# Revit family: Поли-Групп_ЗадвижкаКлиноваяEAZ-МК-F5(ВS)_DN350-1600
name_source: partatom
category: Арматура трубопроводов
units: mm (PartAtom-declared; Revit-internal decimal feet)

## family parameters
Всегда вертикально = Да
На основе рабочей плоскости = Нет
Общий = Нет
При загрузке вырезать с полостями = Нет
Размер круглого соединителя = Использовать диаметр
Тип детали = Клапан - Вставляется

## types (24) — shared parameters
ADSK_URL страницы изделия = https://www.polycorr.ru
ADSK_Версия Revit = 2019
ADSK_Единица измерения = шт
ADSK_Завод-изготовитель = ООО ПК «Поли-Групп»
ADSK_Количество = 1
ADSK_Материал = Высокопрочный чугун GGG-40
ADSK_Материал наименование = Высокопрочный чугун с шаровидным графитом (GGG-40)
Kv = 1.0 м³/ч
Класс герметичности = А по ГОСТ Р 9544-2015
Материал Диска = Высокопрочный чугун с шаровидным графитом (GGG-40)
Материал уплотнителя = PTFE
Назначение = Для установки в качестве запорного устройства на трубопроводах
Покрытие = Высококачественное эпоксидное покрытие толщиной 300 мкм
Рабочая среда = Техническая вода, канализационные стоки, морская вода
Разработчик = https://3dbim.pro
Срок службы = 50 лет
ТВ = Поли-Групп_ЗадвижкаКлиноваяEAZ-МК-F5(ВS)_DN350-1600
Температура рабочей среды = 0 до +70°С
Тип привода = Редуктор
Тип присоединения = Фланцевое

## per-type parameters (varying)
- 350-10: A=756 мм; ADSK_Марка=EAZ-GV-3-F5 DN350 PN10; ADSK_Масса=276; ADSK_Масса_Текст=276; ADSK_Наименование=Задвижка клиновая с металлическим уплотнением EAZ MK F5 для сточных вод фланцевая DN350 PN10; ADSK_Наименование краткое=Задвижка клиновая EAZ MK F5 DN350 PN10; D=505 мм; D1=460 мм; D2=429 мм; DN=350 мм; D_Наружный=359 мм; H1=270 мм; H2=976 мм; L=550 мм; L1=270 мм; L2=81 мм; PN=10.0 бары; R=21 мм; R1=206 мм; b=25 мм; d1=88 мм; f=4 мм; h2=683 мм; l1=330 мм; l2=358 мм; l3=495 мм; t=68 мм; Габаритные размеры=505х550х1246; Корпус_Глубина=605 мм; с=18 мм
- 400-10: A=836 мм; ADSK_Марка=EAZ-GV-3-F5 DN400 PN10; ADSK_Масса=330; ADSK_Масса_Текст=330; ADSK_Наименование=Задвижка клиновая с металлическим уплотнением EAZ MK F5 для сточных вод фланцевая DN400 PN10; ADSK_Наименование краткое=Задвижка клиновая EAZ MK F5 DN400 PN10; D=565 мм; D1=515 мм; D2=480 мм; DN=400 мм; D_Наружный=409 мм; H1=300 мм; H2=1068 мм; L=600 мм; L1=300 мм; L2=90 мм; PN=10.0 бары; R=21 мм; R1=206 мм; b=25 мм; d1=100 мм; f=4 мм; h2=748 мм; l1=360 мм; l2=390 мм; l3=540 мм; t=75 мм; Габаритные размеры=565х600х1368; Корпус_Глубина=669 мм; с=18 мм
- 450-10: A=916 мм; ADSK_Марка=EAZ-GV-3-F5 D450 PN10; ADSK_Масса=419; ADSK_Масса_Текст=419; ADSK_Наименование=Задвижка клиновая с металлическим уплотнением EAZ MK F5 для сточных вод фланцевая DN450 PN10; ADSK_Наименование краткое=Задвижка клиновая EAZ MK F5 DN450 PN10; D=615 мм; D1=565 мм; D2=530 мм; DN=450 мм; D_Наружный=459 мм; H1=330 мм; H2=1180 мм; L=650 мм; L1=330 мм; L2=99 мм; PN=10.0 бары; R=28 мм; R1=275 мм; b=26 мм; d1=113 мм; f=4 мм; h2=826 мм; l1=390 мм; l2=423 мм; l3=585 мм; t=83 мм; Габаритные размеры=615х650х1510; Корпус_Глубина=733 мм; с=23 мм
- 500-10: A=996 мм; ADSK_Марка=EAZ-GV-3-F5 DN500 PN10; ADSK_Масса=655; ADSK_Масса_Текст=655; ADSK_Наименование=Задвижка клиновая с металлическим уплотнением EAZ MK F5 для сточных вод фланцевая DN500 PN10; ADSK_Наименование краткое=Задвижка клиновая EAZ MK F5 DN500 PN10; D=670 мм; D1=620 мм; D2=582 мм; DN=500 мм; D_Наружный=509 мм; H1=370 мм; H2=1247 мм; L=700 мм; L1=370 мм; L2=111 мм; PN=10.0 бары; R=28 мм; R1=275 мм; b=27 мм; d1=125 мм; f=4 мм; h2=873 мм; l1=420 мм; l2=455 мм; l3=630 мм; t=87 мм; Габаритные размеры=670х700х1617; Корпус_Глубина=797 мм; с=35 мм
- 600-10: A=1076 мм; ADSK_Марка=EAZ-GV-3-F5 DN600 PN10; ADSK_Масса=775; ADSK_Масса_Текст=775; ADSK_Наименование=Задвижка клиновая с металлическим уплотнением EAZ MK F5 для сточных вод фланцевая DN600 PN10; ADSK_Наименование краткое=Задвижка клиновая EAZ MK F5 DN600 PN10; D=780 мм; D1=725 мм; D2=682 мм; DN=600 мм; D_Наружный=609 мм; H1=430 мм; H2=1416 мм; L=800 мм; L1=430 мм; L2=129 мм; PN=10.0 бары; R=28 мм; R1=275 мм; b=30 мм; d1=150 мм; f=5 мм; h2=991 мм; l1=480 мм; l2=520 мм; l3=720 мм; t=99 мм; Габаритные размеры=780х800х1846; Корпус_Глубина=861 мм; с=40 мм
- 700-10: A=1156 мм; ADSK_Марка=EAZ-GV-3-F5 DN700 PN10; ADSK_Масса=1700; ADSK_Масса_Текст=1700; ADSK_Наименование=Задвижка клиновая с металлическим уплотнением EAZ MK F5 для сточных вод фланцевая DN700 PN10; ADSK_Наименование краткое=Задвижка клиновая EAZ MK F5 DN700 PN10; D=895 мм; D1=840 мм; D2=794 мм; DN=700 мм; D_Наружный=709 мм; H1=495 мм; H2=1808 мм; L=900 мм; L1=495 мм; L2=149 мм; PN=10.0 бары; R=31 мм; R1=307 мм; b=33 мм; d1=175 мм; f=5 мм; h2=1266 мм; l1=540 мм; l2=585 мм; l3=810 мм; t=127 мм; Габаритные размеры=895х900х2303; Корпус_Глубина=925 мм; с=48 мм
- 800-10: A=1242 мм; ADSK_Марка=EAZ-GV-3-F5 DN800 PN10; ADSK_Масса=2245; ADSK_Масса_Текст=2245; ADSK_Наименование=Задвижка клиновая с металлическим уплотнением EAZ MK F5 для сточных вод фланцевая DN800 PN10; ADSK_Наименование краткое=Задвижка клиновая EAZ MK F5 DN800 PN10; D=1015 мм; D1=950 мм; D2=901 мм; DN=800 мм; D_Наружный=809 мм; H1=540 мм; H2=1953 мм; L=1000 мм; L1=540 мм; L2=162 мм; PN=10.0 бары; R=33 мм; R1=330 мм; b=35 мм; d1=200 мм; f=5 мм; h2=1367 мм; l1=600 мм; l2=650 мм; l3=900 мм; t=137 мм; Габаритные размеры=1015х1000х2493; Корпус_Глубина=994 мм; с=33 мм
- 900-10: A=1423 мм; ADSK_Марка=EAZ-GV-3-F5 DN900 PN10; ADSK_Масса=3110; ADSK_Масса_Текст=3110; ADSK_Наименование=Задвижка клиновая с металлическим уплотнением EAZ MK F5 для сточных вод фланцевая DN900 PN10; ADSK_Наименование краткое=Задвижка клиновая EAZ MK F5 DN900 PN10; D=1115 мм; D1=1050 мм; D2=1001 мм; DN=900 мм; D_Наружный=909 мм; H1=645 мм; H2=2132 мм; L=1100 мм; L1=600 мм; L2=180 мм; PN=10.0 бары; R=37 мм; R1=370 мм; b=38 мм; d1=225 мм; f=5 мм; h2=1492 мм; l1=660 мм; l2=715 мм; l3=990 мм; t=149 мм; Габаритные размеры=1115х1100х2777; Корпус_Глубина=1138 мм; с=88 мм
- 1000-10: A=1448 мм; ADSK_Марка=EAZ-GV-3-F5 DN1000 PN10; ADSK_Масса=3510; ADSK_Масса_Текст=3510; ADSK_Наименование=Задвижка клиновая с металлическим уплотнением EAZ MK F5 для сточных вод фланцевая DN1000 PN10; ADSK_Наименование краткое=Задвижка клиновая EAZ MK F5 DN1000 PN10; D=1230 мм; D1=1160 мм; D2=1112 мм; DN=1000 мм; D_Наружный=1009 мм; H1=680 мм; H2=2362 мм; L=1200 мм; L1=680 мм; L2=204 мм; PN=10.0 бары; R=39 мм; R1=390 мм; b=40 мм; d1=250 мм; f=5 мм; h2=1653 мм; l1=720 мм; l2=780 мм; l3=1080 мм; t=165 мм; Габаритные размеры=1230х1200х3042; Корпус_Глубина=1158 мм; с=65 мм
- 1200-10: A=1625 мм; ADSK_Марка=EAZ-GV-3-F5 DN1200 PN10; ADSK_Масса=5180; ADSK_Масса_Текст=5180; ADSK_Наименование=Задвижка клиновая с металлическим уплотнением EAZ MK F5 для сточных вод фланцевая DN1200 PN10; ADSK_Наименование краткое=Задвижка клиновая EAZ MK F5 DN1200 PN10; D=1455 мм; D1=1380 мм; D2=1328 мм; DN=1200 мм; D_Наружный=1209 мм; H1=800 мм; H2=2652 мм; L=1400 мм; L1=800 мм; L2=240 мм; PN=10.0 бары; R=43 мм; R1=430 мм; b=45 мм; d1=300 мм; f=5 мм; h2=1856 мм; l1=840 мм; l2=910 мм; l3=1260 мм; t=186 мм; Габаритные размеры=1455х1400х3452; Корпус_Глубина=1300 мм; с=73 мм
- 1400-10: A=1860 мм; ADSK_Марка=EAZ-GV-3-F5 DN1400 PN10; ADSK_Масса=7128; ADSK_Масса_Текст=7128; ADSK_Наименование=Задвижка клиновая с металлическим уплотнением EAZ MK F5 для сточных вод фланцевая DN1400 PN10; ADSK_Наименование краткое=Задвижка клиновая EAZ MK F5 DN1400 PN10; D=1675 мм; D1=1590 мм; D2=1530 мм; DN=1400 мм; D_Наружный=1409 мм; H1=870 мм; H2=2972 мм; L=1600 мм; L1=870 мм; L2=261 мм; PN=10.0 бары; R=51 мм; R1=510 мм; b=46 мм; d1=350 мм; f=5 мм; h2=2080 мм; l1=960 мм; l2=1040 мм; l3=1440 мм; t=208 мм; Габаритные размеры=1675х1600х3842; Корпус_Глубина=1488 мм; с=33 мм
- 1600-10: A=2065 мм; ADSK_Марка=EAZ-GV-3-F5 DN1600 PN10; ADSK_Масса=10200; ADSK_Масса_Текст=10200; ADSK_Наименование=Задвижка клиновая с металлическим уплотнением EAZ MK F5 для сточных вод фланцевая DN1600 PN10; ADSK_Наименование краткое=Задвижка клиновая EAZ MK F5 DN1600 PN10; D=1915 мм; D1=1820 мм; D2=1750 мм; DN=1600 мм; D_Наружный=1609 мм; H1=1000 мм; H2=3380 мм; L=1600 мм; L1=1000 мм; L2=300 мм; PN=10.0 бары; R=63 мм; R1=630 мм; b=49 мм; d1=400 мм; f=5 мм; h2=2366 мм; l1=960 мм; l2=1040 мм; l3=1440 мм; t=237 мм; Габаритные размеры=1915х1600х4380; Корпус_Глубина=1652 мм; с=43 мм
- 350-16: A=756 мм; ADSK_Марка=EAZ-GV-3-F5 DN350 PN16; ADSK_Масса=285; ADSK_Масса_Текст=285; ADSK_Наименование=Задвижка клиновая с металлическим уплотнением EAZ MK F5 для сточных вод фланцевая DN350 PN16; ADSK_Наименование краткое=Задвижка клиновая EAZ MK F5 DN350 PN16; D=520 мм; D1=470 мм; D2=429 мм; DN=350 мм; D_Наружный=359 мм; H1=270 мм; H2=976 мм; L=550 мм; L1=270 мм; L2=81 мм; PN=16.0 бары; R=21 мм; R1=206 мм; b=27 мм; d1=88 мм; f=4 мм; h2=683 мм; l1=330 мм; l2=358 мм; l3=495 мм; t=68 мм; Габаритные размеры=520х550х1246; Корпус_Глубина=605 мм; с=10 мм
- 400-16: A=836 мм; ADSK_Марка=EAZ-GV-3-F5 DN400 PN16; ADSK_Масса=335; ADSK_Масса_Текст=335; ADSK_Наименование=Задвижка клиновая с металлическим уплотнением EAZ MK F5 для сточных вод фланцевая DN400 PN16; ADSK_Наименование краткое=Задвижка клиновая EAZ MK F5 DN400 PN16; D=580 мм; D1=525 мм; D2=480 мм; DN=400 мм; D_Наружный=409 мм; H1=300 мм; H2=1068 мм; L=600 мм; L1=300 мм; L2=90 мм; PN=16.0 бары; R=21 мм; R1=206 мм; b=28 мм; d1=100 мм; f=4 мм; h2=748 мм; l1=360 мм; l2=390 мм; l3=540 мм; t=75 мм; Габаритные размеры=580х600х1368; Корпус_Глубина=669 мм; с=10 мм
- 450-16: A=916 мм; ADSK_Марка=EAZ-GV-3-F5 DN450 PN16; ADSK_Масса=425; ADSK_Масса_Текст=425; ADSK_Наименование=Задвижка клиновая с металлическим уплотнением EAZ MK F5 для сточных вод фланцевая DN450 PN16; ADSK_Наименование краткое=Задвижка клиновая EAZ MK F5 DN450 PN16; D=640 мм; D1=585 мм; D2=548 мм; DN=450 мм; D_Наружный=459 мм; H1=330 мм; H2=1180 мм; L=650 мм; L1=330 мм; L2=99 мм; PN=16.0 бары; R=28 мм; R1=275 мм; b=30 мм; d1=113 мм; f=4 мм; h2=826 мм; l1=390 мм; l2=423 мм; l3=585 мм; t=83 мм; Габаритные размеры=640х650х1510; Корпус_Глубина=733 мм; с=10 мм
- 500-16: A=996 мм; ADSK_Марка=EAZ-GV-3-F5 DN500 PN16; ADSK_Масса=668; ADSK_Масса_Текст=668; ADSK_Наименование=Задвижка клиновая с металлическим уплотнением EAZ MK F5 для сточных вод фланцевая DN500 PN16; ADSK_Наименование краткое=Задвижка клиновая EAZ MK F5 DN500 PN16; D=715 мм; D1=650 мм; D2=609 мм; DN=500 мм; D_Наружный=509 мм; H1=370 мм; H2=1247 мм; L=700 мм; L1=370 мм; L2=111 мм; PN=16.0 бары; R=28 мм; R1=275 мм; b=32 мм; d1=125 мм; f=4 мм; h2=873 мм; l1=420 мм; l2=455 мм; l3=630 мм; t=87 мм; Габаритные размеры=715х700х1617; Корпус_Глубина=797 мм; с=13 мм
- 600-16: A=1076 мм; ADSK_Марка=EAZ-GV-3-F5 DN600 PN16; ADSK_Масса=790; ADSK_Масса_Текст=790; ADSK_Наименование=Задвижка клиновая с металлическим уплотнением EAZ MK F5 для сточных вод фланцевая DN600 PN16; ADSK_Наименование краткое=Задвижка клиновая EAZ MK F5 DN600 PN16; D=840 мм; D1=770 мм; D2=720 мм; DN=600 мм; D_Наружный=609 мм; H1=430 мм; H2=1416 мм; L=800 мм; L1=430 мм; L2=129 мм; PN=16.0 бары; R=28 мм; R1=275 мм; b=36 мм; d1=150 мм; f=5 мм; h2=991 мм; l1=480 мм; l2=520 мм; l3=720 мм; t=99 мм; Габаритные размеры=840х800х1846; Корпус_Глубина=861 мм; с=10 мм
- 700-16: A=1156 мм; ADSK_Марка=EAZ-GV-3-F5 DN700 PN16; ADSK_Масса=1765; ADSK_Масса_Текст=1765; ADSK_Наименование=Задвижка клиновая с металлическим уплотнением EAZ MK F5 для сточных вод фланцевая DN700 PN16; ADSK_Наименование краткое=Задвижка клиновая EAZ MK F5 DN700 PN16; D=910 мм; D1=840 мм; D2=794 мм; DN=700 мм; D_Наружный=709 мм; H1=495 мм; H2=1808 мм; L=900 мм; L1=495 мм; L2=149 мм; PN=16.0 бары; R=31 мм; R1=307 мм; b=40 мм; d1=175 мм; f=5 мм; h2=1266 мм; l1=540 мм; l2=585 мм; l3=810 мм; t=127 мм; Габаритные размеры=910х900х2303; Корпус_Глубина=925 мм; с=40 мм
- 800-16: A=1242 мм; ADSK_Марка=EAZ-GV-3-F5 DN800 PN16; ADSK_Масса=2460; ADSK_Масса_Текст=2460; ADSK_Наименование=Задвижка клиновая с металлическим уплотнением EAZ MK F5 для сточных вод фланцевая DN800 PN16; ADSK_Наименование краткое=Задвижка клиновая EAZ MK F5 DN800 PN16; D=1025 мм; D1=950 мм; D2=901 мм; DN=800 мм; D_Наружный=809 мм; H1=540 мм; H2=1953 мм; L=1000 мм; L1=540 мм; L2=162 мм; PN=16.0 бары; R=33 мм; R1=330 мм; b=43 мм; d1=200 мм; f=5 мм; h2=1367 мм; l1=600 мм; l2=650 мм; l3=900 мм; t=137 мм; Габаритные размеры=1025х1000х2493; Корпус_Глубина=994 мм; с=28 мм
- 900-16: A=1423 мм; ADSK_Марка=EAZ-GV-3-F5 DN900 PN16; ADSK_Масса=3160; ADSK_Масса_Текст=3160; ADSK_Наименование=Задвижка клиновая с металлическим уплотнением EAZ MK F5 для сточных вод фланцевая DN900 PN16; ADSK_Наименование краткое=Задвижка клиновая EAZ MK F5 DN900 PN16; D=1125 мм; D1=1050 мм; D2=1001 мм; DN=900 мм; D_Наружный=909 мм; H1=645 мм; H2=2132 мм; L=1100 мм; L1=600 мм; L2=180 мм; PN=16.0 бары; R=37 мм; R1=370 мм; b=47 мм; d1=225 мм; f=5 мм; h2=1492 мм; l1=660 мм; l2=715 мм; l3=990 мм; t=149 мм; Габаритные размеры=1125х1100х2777; Корпус_Глубина=1138 мм; с=83 мм
- 1000-16: A=1448 мм; ADSK_Марка=EAZ-GV-3-F5 DN1000 PN16; ADSK_Масса=3625; ADSK_Масса_Текст=3625; ADSK_Наименование=Задвижка клиновая с металлическим уплотнением EAZ MK F5 для сточных вод фланцевая DN1000 PN16; ADSK_Наименование краткое=Задвижка клиновая EAZ MK F5 DN1000 PN16; D=1255 мм; D1=1160 мм; D2=1112 мм; DN=1000 мм; D_Наружный=1009 мм; H1=680 мм; H2=2362 мм; L=1200 мм; L1=680 мм; L2=204 мм; PN=16.0 бары; R=39 мм; R1=390 мм; b=50 мм; d1=250 мм; f=5 мм; h2=1653 мм; l1=720 мм; l2=780 мм; l3=1080 мм; t=165 мм; Габаритные размеры=1255х1200х3042; Корпус_Глубина=1158 мм; с=53 мм
- 1200-16: A=1625 мм; ADSK_Марка=EAZ-GV-3-F5 DN1200 PN16; ADSK_Масса=5250; ADSK_Масса_Текст=5250; ADSK_Наименование=Задвижка клиновая с металлическим уплотнением EAZ MK F5 для сточных вод фланцевая DN1200 PN16; ADSK_Наименование краткое=Задвижка клиновая EAZ MK F5 DN1200 PN16; D=1485 мм; D1=1380 мм; D2=1328 мм; DN=1200 мм; D_Наружный=1209 мм; H1=800 мм; H2=2652 мм; L=1400 мм; L1=800 мм; L2=240 мм; PN=16.0 бары; R=43 мм; R1=430 мм; b=57 мм; d1=300 мм; f=5 мм; h2=1856 мм; l1=840 мм; l2=910 мм; l3=1260 мм; t=186 мм; Габаритные размеры=1485х1400х3452; Корпус_Глубина=1300 мм; с=58 мм
- 1400-16: A=1860 мм; ADSK_Марка=EAZ-GV-3-F5 DN1400 PN16; ADSK_Масса=7980; ADSK_Масса_Текст=7980; ADSK_Наименование=Задвижка клиновая с металлическим уплотнением EAZ MK F5 для сточных вод фланцевая DN1400 PN16; ADSK_Наименование краткое=Задвижка клиновая EAZ MK F5 DN1400 PN16; D=1685 мм; D1=1590 мм; D2=1530 мм; DN=1400 мм; D_Наружный=1409 мм; H1=870 мм; H2=3010 мм; L=1600 мм; L1=870 мм; L2=261 мм; PN=16.0 бары; R=51 мм; R1=510 мм; b=60 мм; d1=350 мм; f=5 мм; h2=2107 мм; l1=960 мм; l2=1040 мм; l3=1440 мм; t=211 мм; Габаритные размеры=1685х1600х3880; Корпус_Глубина=1488 мм; с=28 мм
- 1600-16: A=2065 мм; ADSK_Марка=EAZ-GV-3-F5 DN1600 PN16; ADSK_Масса=10500; ADSK_Масса_Текст=10500; ADSK_Наименование=Задвижка клиновая с металлическим уплотнением EAZ MK F5 для сточных вод фланцевая DN1600 PN16; ADSK_Наименование краткое=Задвижка клиновая EAZ MK F5 DN1600 PN16; D=1930 мм; D1=1820 мм; D2=1750 мм; DN=1600 мм; D_Наружный=1609 мм; H1=1000 мм; H2=3410 мм; L=1600 мм; L1=1000 мм; L2=300 мм; PN=16.0 бары; R=63 мм; R1=630 мм; b=65 мм; d1=400 мм; f=5 мм; h2=2387 мм; l1=960 мм; l2=1040 мм; l3=1440 мм; t=239 мм; Габаритные размеры=1930х1600х4410; Корпус_Глубина=1652 мм; с=35 мм
